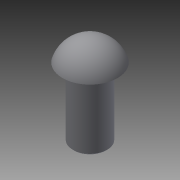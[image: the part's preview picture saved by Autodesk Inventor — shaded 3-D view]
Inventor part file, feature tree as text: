
AUTODESK INVENTOR PART (.ipt)
format: ipt  version: 2015 (Build 190159000, 159)  size: 100,864 bytes
history: native  units: in
note: dims shown in document units (in); Inventor stores cm internally (conversion verified against a paired STEP export)
features: revolve x1, chamfer x1, sketch x1
ambient origin geometry x8: Origin, YZ Plane, XZ Plane, XY Plane, X Axis, Y Axis, Z Axis, Center Point
bodies: Solid1 (feature_tree)
feature tree (3):
  revolve  "Revolution1"  [1 undecoded]
  chamfer  "Chamfer1"  Distance=0.208in
  sketch  "Sketch1"  dims[d0=0.5in d1=0.65in d2=0.208in d3=0.075in d4=0.125in d5=90.0deg d6=0.01in d7=0.125in d8=45.0deg]
note: 1 required parameter value undecoded (feature->parameter linkage not recoverable at this tier; creation-order binding heuristic only, values carry confidence <= 0.55)
